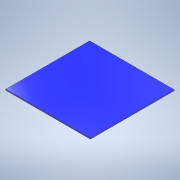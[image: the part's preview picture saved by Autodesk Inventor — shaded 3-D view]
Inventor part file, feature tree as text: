
AUTODESK INVENTOR PART (.ipt)
format: ipt  version: 2022 (Build 260153000, 153)  size: 102,400 bytes
history: native  units: in
note: dims shown in document units (in); Inventor stores cm internally (conversion verified against a paired STEP export)
features: extrude x1, sketch x1
ambient origin geometry x8: Origin, YZ Plane, XZ Plane, XY Plane, X Axis, Y Axis, Z Axis, Center Point
bodies: Solid1 (feature_tree)
feature tree (2):
  extrude  "Extrusion1"  Depth=0.8504in
  sketch  "Sketch1"  dims[d0=0.8425in d1=0.8504in d2=0.0118in d3=0.0in]
